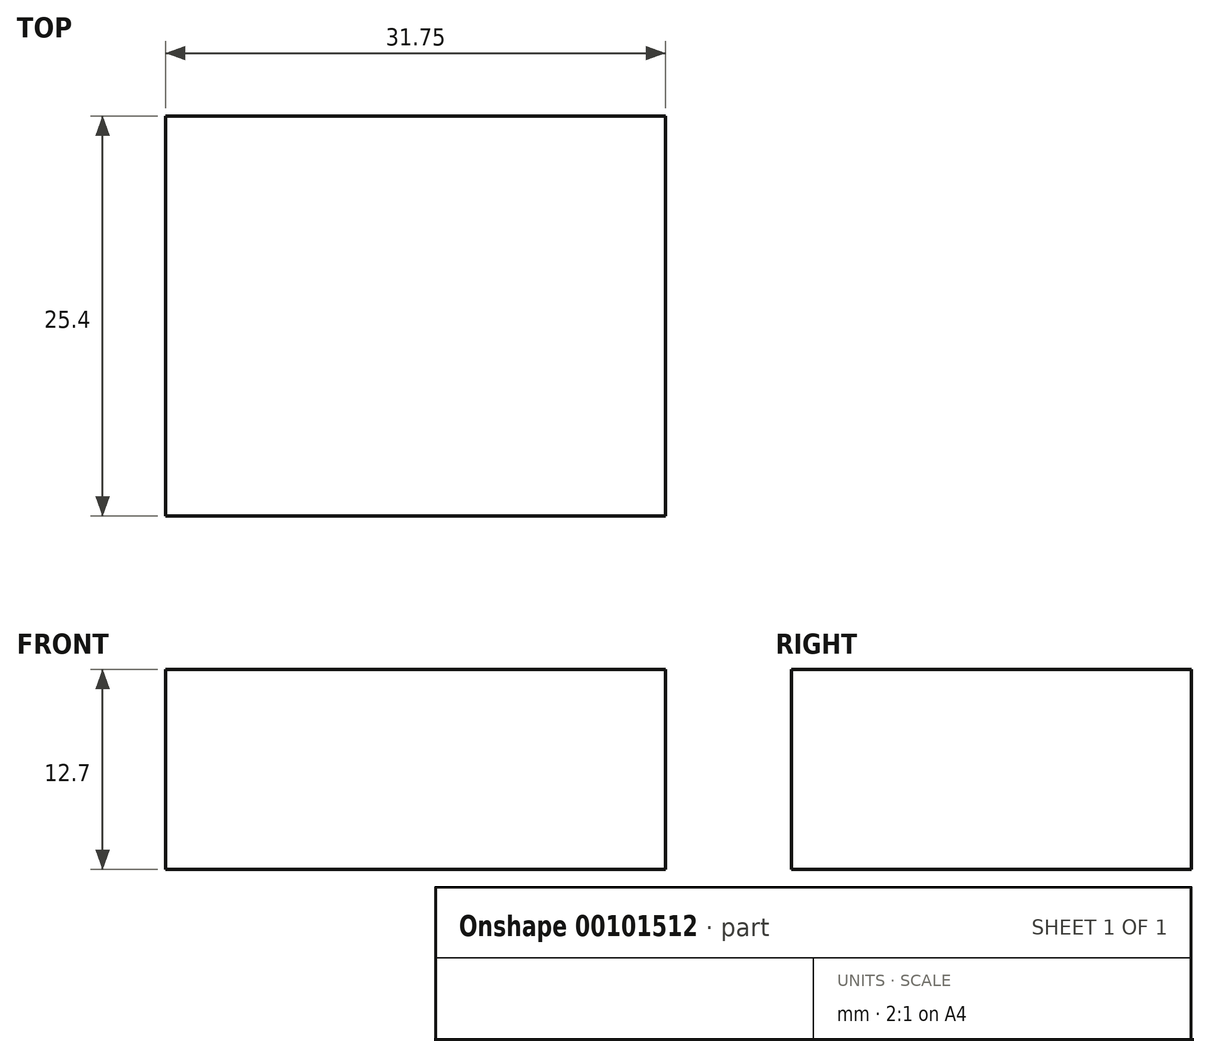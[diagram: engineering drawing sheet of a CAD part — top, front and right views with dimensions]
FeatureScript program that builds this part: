
annotation { "Feature Type Name" : "Feature", "Feature Type Description" : "" }
export const myFeature = defineFeature(function(context is Context, id is Id, definition is map)
    precondition{}
    {
        {
            var Q0;
            Q0=qCreatedBy(makeId("Front.planeOp"),FACE);
            var sketch = newSketch(context, id + "F0", { "sketchPlane" : qUnion([Q0])});
            skLineSegment(sketch, "E0.bottom", {"start": v(0, 0) * mm, "end": v(38.1, 0) * mm});
            skLineSegment(sketch, "E0.top", {"start": v(0, -25.4) * mm, "end": v(38.1, -25.4) * mm});
            skLineSegment(sketch, "E0.left", {"start": v(0, 0) * mm, "end": v(0, -25.4) * mm});
            skLineSegment(sketch, "E0.right", {"start": v(38.1, 0) * mm, "end": v(38.1, -25.4) * mm});
            skLineSegment(sketch, "E1.bottom", {"start": v(38.1, 0) * mm, "end": v(6.35, 0) * mm});
            skLineSegment(sketch, "E1.top", {"start": v(38.1, -12.7) * mm, "end": v(6.35, -12.7) * mm});
            skLineSegment(sketch, "E1.left", {"start": v(38.1, 0) * mm, "end": v(38.1, -12.7) * mm});
            skLineSegment(sketch, "E1.right", {"start": v(6.35, 0) * mm, "end": v(6.35, -12.7) * mm});
            skSolve(sketch);
        }
        {
            var Q0;
            Q0=makeQuery(id+"F0.imprint","IMPRINT",FACE,{"disambiguationData":[TD([[makeQuery(id+"F0.imprint","IMPRINT",EDGE,{"derivedFrom":sQuery(id+"F0.wireOp",EDGE,"E0.bottom")}),-1.0]])]});
            extrude(context, id + "F1", {"entities" : qUnion([Q0]), "depth" : 25.4 * mm});
        }
    });
